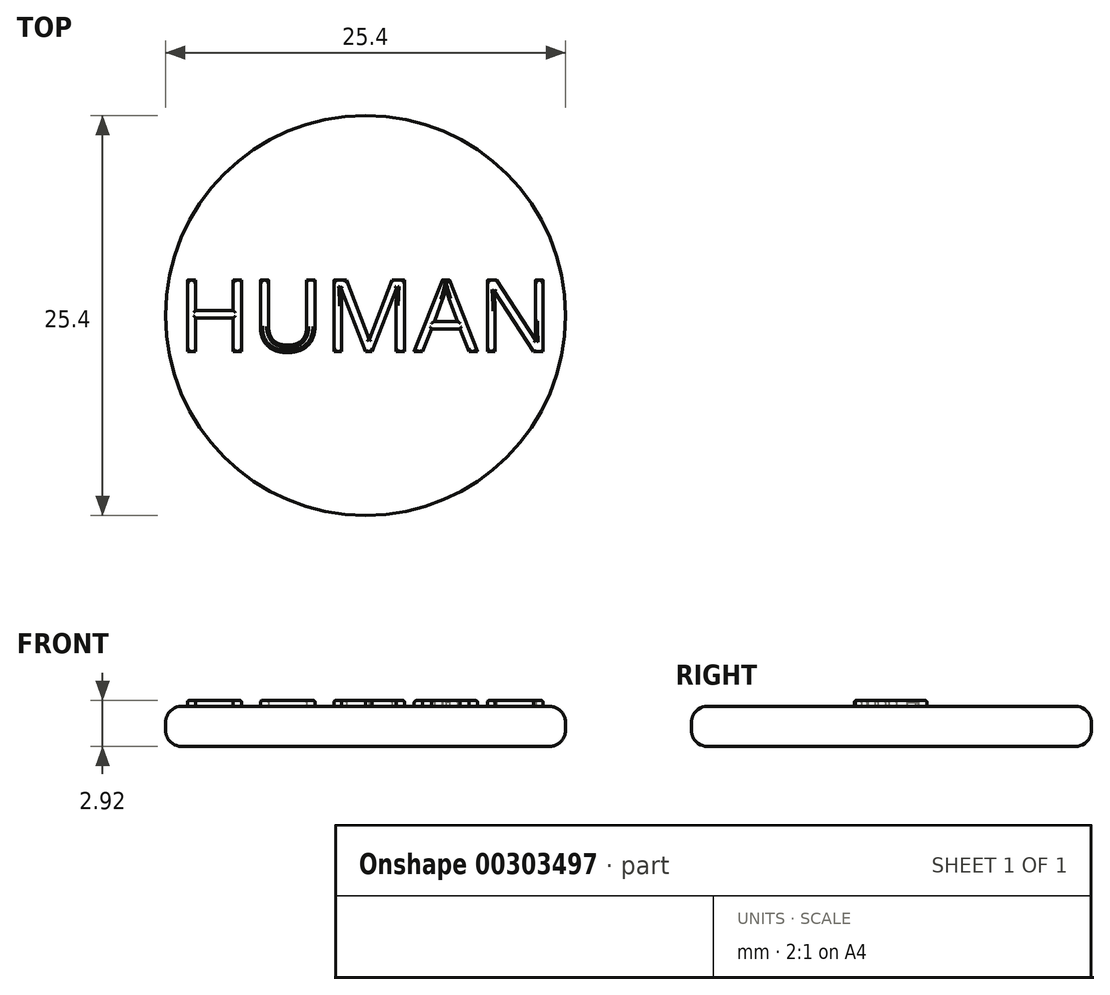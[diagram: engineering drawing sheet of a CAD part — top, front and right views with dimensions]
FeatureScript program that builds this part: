
annotation { "Feature Type Name" : "Feature", "Feature Type Description" : "" }
export const myFeature = defineFeature(function(context is Context, id is Id, definition is map)
    precondition{}
    {
        {
            var Q0;
            Q0=qCreatedBy(makeId("Top.planeOp"),FACE);
            var sketch = newSketch(context, id + "F0", { "sketchPlane" : qUnion([Q0])});
            skCircle(sketch, "E0", {"center": v(0, 0) * mm, "radius": 12.7 * mm});
            skLineSegment(sketch, "E1", {"start": v(0, 0) * mm, "end": v(-11.94, 0) * mm});
            skLineSegment(sketch, "E2", {"start": v(-11.94, 0) * mm, "end": v(-11.94, 2.29) * mm});
            skLineSegment(sketch, "E3", {"start": v(-11.94, 0) * mm, "end": v(-11.94, -2.29) * mm});
            skText(sketch, "E4", { "text": "HUMAN", "fontName": "OpenSans-Regular.ttf"});
            const initialGuessF0  = {"E4": [-0.01194, -0.00229, 1, 0, 0.00457]};
            skSetInitialGuess(sketch, initialGuessF0);
            skSolve(sketch);
        }
        {
            var Q0;
            Q0=makeQuery(id+"F0.imprint","IMPRINT",FACE,{"disambiguationData":[TD([[makeQuery(id+"F0.imprint","IMPRINT",EDGE,{"derivedFrom":sQuery(id+"F0.wireOp",EDGE,"E0")}),1.0]])]});
            var Q1;
            {var subQ0=sQuery(id+"F0.wireOp",EDGE,"E4.sketch_text.stroke-20");Q1=makeQuery(id+"F0.imprint","IMPRINT",FACE,{"disambiguationData":[TD([[makeQuery(id+"F0.imprint","IMPRINT",EDGE,{"derivedFrom":subQ0}),1.0]])]});}
            var Q2;
            {var subQ1=sQuery(id+"F0.wireOp",EDGE,"E4.sketch_text.stroke-27");Q2=makeQuery(id+"F0.imprint","IMPRINT",FACE,{"disambiguationData":[TD([[makeQuery(id+"F0.imprint","IMPRINT",EDGE,{"derivedFrom":subQ1}),1.0]])]});}
            var Q3;
            Q3=makeQuery(id+"F0.imprint","IMPRINT",FACE,{"disambiguationData":[TD([[makeQuery(id+"F0.imprint","IMPRINT",EDGE,{"derivedFrom":sQuery(id+"F0.wireOp",EDGE,"E4.sketch_text.stroke-52")}),1.0]])]});
            extrude(context, id + "F1", {"entities" : qUnion([Q0, Q1, Q2, Q3]), "depth" : 2.54 * mm});
        }
        {
            var Q0;
            {var subQ0=sQuery(id+"F0.wireOp",EDGE,"E4.sketch_text.stroke-6");Q0=makeQuery(id+"F0.imprint","IMPRINT",FACE,{"disambiguationData":[TD([[makeQuery(id+"F0.imprint","IMPRINT",EDGE,{"derivedFrom":subQ0}),-1.0]])]});}
            var Q1;
            {var subQ1=sQuery(id+"F0.wireOp",EDGE,"E4.sketch_text.stroke-0");Q1=makeQuery(id+"F0.imprint","IMPRINT",FACE,{"disambiguationData":[TD([[makeQuery(id+"F0.imprint","IMPRINT",EDGE,{"derivedFrom":subQ1}),-1.0]])]});}
            var Q2;
            {var subQ9=sQuery(id+"F0.wireOp",EDGE,"E4.sketch_text.stroke-13");Q2=makeQuery(id+"F0.imprint","IMPRINT",FACE,{"disambiguationData":[TD([[makeQuery(id+"F0.imprint","IMPRINT",EDGE,{"derivedFrom":subQ9}),-1.0]])]});}
            var Q3;
            {var subQ5=sQuery(id+"F0.wireOp",EDGE,"E4.sketch_text.stroke-18");Q3=makeQuery(id+"F0.imprint","IMPRINT",FACE,{"disambiguationData":[TD([[makeQuery(id+"F0.imprint","IMPRINT",EDGE,{"derivedFrom":subQ5}),-1.0]])]});}
            var Q4;
            {var subQ5=sQuery(id+"F0.wireOp",EDGE,"E4.sketch_text.stroke-25");Q4=makeQuery(id+"F0.imprint","IMPRINT",FACE,{"disambiguationData":[TD([[makeQuery(id+"F0.imprint","IMPRINT",EDGE,{"derivedFrom":subQ5}),-1.0]])]});}
            var Q5;
            {var subQ0=sQuery(id+"F0.wireOp",EDGE,"E4.sketch_text.stroke-27");Q5=makeQuery(id+"F0.imprint","IMPRINT",FACE,{"disambiguationData":[TD([[makeQuery(id+"F0.imprint","IMPRINT",EDGE,{"derivedFrom":subQ0}),-1.0]])]});}
            var Q6;
            {var subQ5=sQuery(id+"F0.wireOp",EDGE,"E4.sketch_text.stroke-30");Q6=makeQuery(id+"F0.imprint","IMPRINT",FACE,{"disambiguationData":[TD([[makeQuery(id+"F0.imprint","IMPRINT",EDGE,{"derivedFrom":subQ5}),-1.0]])]});}
            var Q7;
            {var subQ5=sQuery(id+"F0.wireOp",EDGE,"E4.sketch_text.stroke-34");Q7=makeQuery(id+"F0.imprint","IMPRINT",FACE,{"disambiguationData":[TD([[makeQuery(id+"F0.imprint","IMPRINT",EDGE,{"derivedFrom":subQ5}),-1.0]])]});}
            var Q8;
            Q8=makeQuery(id+"F0.imprint","IMPRINT",FACE,{"disambiguationData":[TD([[makeQuery(id+"F0.imprint","IMPRINT",EDGE,{"derivedFrom":sQuery(id+"F0.wireOp",EDGE,"E4.sketch_text.stroke-44")}),-1.0]])]});
            var Q9;
            Q9=makeQuery(id+"F0.imprint","IMPRINT",FACE,{"disambiguationData":[TD([[makeQuery(id+"F0.imprint","IMPRINT",EDGE,{"derivedFrom":sQuery(id+"F0.wireOp",EDGE,"E4.sketch_text.stroke-57")}),-1.0]])]});
            extrude(context, id + "F2", {"entities" : qUnion([Q0, Q1, Q2, Q3, Q4, Q5, Q6, Q7, Q8, Q9]), "depth" : 2.92 * mm, "hasSecondDirection" : true, "secondDirectionOppositeDirection" : false, "secondDirectionDepth" : 0.64 * mm});
        }
        {
            var Q0;
            Q0=makeQuery(id+"F2.opExtrude","CAP_FACE",FACE,{"disambiguationData":[OSD([sQuery(id+"F0.wireOp",EDGE,"E4.sketch_text.stroke-0"),sQuery(id+"F0.wireOp",EDGE,"E4.sketch_text.stroke-1"),sQuery(id+"F0.wireOp",EDGE,"E4.sketch_text.stroke-2"),sQuery(id+"F0.wireOp",EDGE,"E4.sketch_text.stroke-3"),sQuery(id+"F0.wireOp",EDGE,"E4.sketch_text.stroke-4"),sQuery(id+"F0.wireOp",EDGE,"E4.sketch_text.stroke-5"),sQuery(id+"F0.wireOp",EDGE,"E4.sketch_text.stroke-6"),sQuery(id+"F0.wireOp",EDGE,"E4.sketch_text.stroke-7"),sQuery(id+"F0.wireOp",EDGE,"E4.sketch_text.stroke-8"),sQuery(id+"F0.wireOp",EDGE,"E4.sketch_text.stroke-9"),sQuery(id+"F0.wireOp",EDGE,"E4.sketch_text.stroke-10"),sQuery(id+"F0.wireOp",EDGE,"E4.sketch_text.stroke-11")])],"isStart":false});
            var Q1;
            Q1=makeQuery(id+"F2.opExtrude","CAP_FACE",FACE,{"disambiguationData":[OSD([sQuery(id+"F0.wireOp",EDGE,"E4.sketch_text.stroke-12"),sQuery(id+"F0.wireOp",EDGE,"E4.sketch_text.stroke-13"),sQuery(id+"F0.wireOp",EDGE,"E4.sketch_text.stroke-14"),sQuery(id+"F0.wireOp",EDGE,"E4.sketch_text.stroke-15"),sQuery(id+"F0.wireOp",EDGE,"E4.sketch_text.stroke-16"),sQuery(id+"F0.wireOp",EDGE,"E4.sketch_text.stroke-17"),sQuery(id+"F0.wireOp",EDGE,"E4.sketch_text.stroke-18"),sQuery(id+"F0.wireOp",EDGE,"E4.sketch_text.stroke-19"),sQuery(id+"F0.wireOp",EDGE,"E4.sketch_text.stroke-20"),sQuery(id+"F0.wireOp",EDGE,"E4.sketch_text.stroke-21"),sQuery(id+"F0.wireOp",EDGE,"E4.sketch_text.stroke-22"),sQuery(id+"F0.wireOp",EDGE,"E4.sketch_text.stroke-23"),sQuery(id+"F0.wireOp",EDGE,"E4.sketch_text.stroke-24"),sQuery(id+"F0.wireOp",EDGE,"E4.sketch_text.stroke-25")])],"isStart":false});
            var Q2;
            Q2=makeQuery(id+"F2.opExtrude","CAP_FACE",FACE,{"disambiguationData":[OSD([sQuery(id+"F0.wireOp",EDGE,"E4.sketch_text.stroke-26"),sQuery(id+"F0.wireOp",EDGE,"E4.sketch_text.stroke-27"),sQuery(id+"F0.wireOp",EDGE,"E4.sketch_text.stroke-28"),sQuery(id+"F0.wireOp",EDGE,"E4.sketch_text.stroke-29"),sQuery(id+"F0.wireOp",EDGE,"E4.sketch_text.stroke-30"),sQuery(id+"F0.wireOp",EDGE,"E4.sketch_text.stroke-31"),sQuery(id+"F0.wireOp",EDGE,"E4.sketch_text.stroke-32"),sQuery(id+"F0.wireOp",EDGE,"E4.sketch_text.stroke-33"),sQuery(id+"F0.wireOp",EDGE,"E4.sketch_text.stroke-34"),sQuery(id+"F0.wireOp",EDGE,"E4.sketch_text.stroke-35"),sQuery(id+"F0.wireOp",EDGE,"E4.sketch_text.stroke-36"),sQuery(id+"F0.wireOp",EDGE,"E4.sketch_text.stroke-37"),sQuery(id+"F0.wireOp",EDGE,"E4.sketch_text.stroke-38"),sQuery(id+"F0.wireOp",EDGE,"E4.sketch_text.stroke-39"),sQuery(id+"F0.wireOp",EDGE,"E4.sketch_text.stroke-40"),sQuery(id+"F0.wireOp",EDGE,"E4.sketch_text.stroke-41"),sQuery(id+"F0.wireOp",EDGE,"E4.sketch_text.stroke-42"),sQuery(id+"F0.wireOp",EDGE,"E4.sketch_text.stroke-43")])],"isStart":false});
            var Q3;
            Q3=makeQuery(id+"F2.opExtrude","CAP_FACE",FACE,{"disambiguationData":[OSD([sQuery(id+"F0.wireOp",EDGE,"E4.sketch_text.stroke-44"),sQuery(id+"F0.wireOp",EDGE,"E4.sketch_text.stroke-45"),sQuery(id+"F0.wireOp",EDGE,"E4.sketch_text.stroke-46"),sQuery(id+"F0.wireOp",EDGE,"E4.sketch_text.stroke-47"),sQuery(id+"F0.wireOp",EDGE,"E4.sketch_text.stroke-48"),sQuery(id+"F0.wireOp",EDGE,"E4.sketch_text.stroke-49"),sQuery(id+"F0.wireOp",EDGE,"E4.sketch_text.stroke-50"),sQuery(id+"F0.wireOp",EDGE,"E4.sketch_text.stroke-51"),sQuery(id+"F0.wireOp",EDGE,"E4.sketch_text.stroke-52"),sQuery(id+"F0.wireOp",EDGE,"E4.sketch_text.stroke-53"),sQuery(id+"F0.wireOp",EDGE,"E4.sketch_text.stroke-54"),sQuery(id+"F0.wireOp",EDGE,"E4.sketch_text.stroke-55"),sQuery(id+"F0.wireOp",EDGE,"E4.sketch_text.stroke-56")])],"isStart":false});
            var Q4;
            Q4=makeQuery(id+"F2.opExtrude","CAP_FACE",FACE,{"disambiguationData":[OSD([sQuery(id+"F0.wireOp",EDGE,"E4.sketch_text.stroke-57"),sQuery(id+"F0.wireOp",EDGE,"E4.sketch_text.stroke-58"),sQuery(id+"F0.wireOp",EDGE,"E4.sketch_text.stroke-59"),sQuery(id+"F0.wireOp",EDGE,"E4.sketch_text.stroke-60"),sQuery(id+"F0.wireOp",EDGE,"E4.sketch_text.stroke-61"),sQuery(id+"F0.wireOp",EDGE,"E4.sketch_text.stroke-62"),sQuery(id+"F0.wireOp",EDGE,"E4.sketch_text.stroke-63"),sQuery(id+"F0.wireOp",EDGE,"E4.sketch_text.stroke-64"),sQuery(id+"F0.wireOp",EDGE,"E4.sketch_text.stroke-65"),sQuery(id+"F0.wireOp",EDGE,"E4.sketch_text.stroke-66"),sQuery(id+"F0.wireOp",EDGE,"E4.sketch_text.stroke-67"),sQuery(id+"F0.wireOp",EDGE,"E4.sketch_text.stroke-68"),sQuery(id+"F0.wireOp",EDGE,"E4.sketch_text.stroke-69"),sQuery(id+"F0.wireOp",EDGE,"E4.sketch_text.stroke-70"),sQuery(id+"F0.wireOp",EDGE,"E4.sketch_text.stroke-71")])],"isStart":false});
            fillet(context, id + "F3", {"entities" : qUnion([Q0, Q1, Q2, Q3, Q4]), "radius" : 0.13 * mm, "tangentPropagation" : true, "allowEdgeOverflow" : false});
        }
        {
            var Q0;
            Q0=makeQuery(id+"F1.opExtrude","CAP_EDGE",EDGE,{"disambiguationData":[OSD([sQuery(id+"F0.wireOp",EDGE,"E0")])],"isStart":false});
            var Q1;
            Q1=makeQuery(id+"F1.opExtrude","SWEPT_FACE",FACE,{"disambiguationData":[OSD([sQuery(id+"F0.wireOp",EDGE,"E0")])]});
            fillet(context, id + "F4", {"entities" : qUnion([Q0, Q1]), "radius" : 1.02 * mm, "tangentPropagation" : true, "allowEdgeOverflow" : false});
        }
        {
            var Q0;
            {var subQ0=sQuery(id+"F0.wireOp",EDGE,"E4.sketch_text.stroke-6");Q0=makeQuery(id+"F0.imprint","IMPRINT",FACE,{"disambiguationData":[TD([[makeQuery(id+"F0.imprint","IMPRINT",EDGE,{"derivedFrom":subQ0}),-1.0]])]});}
            var Q1;
            {var subQ1=sQuery(id+"F0.wireOp",EDGE,"E4.sketch_text.stroke-0");Q1=makeQuery(id+"F0.imprint","IMPRINT",FACE,{"disambiguationData":[TD([[makeQuery(id+"F0.imprint","IMPRINT",EDGE,{"derivedFrom":subQ1}),-1.0]])]});}
            var Q2;
            {var subQ9=sQuery(id+"F0.wireOp",EDGE,"E4.sketch_text.stroke-13");Q2=makeQuery(id+"F0.imprint","IMPRINT",FACE,{"disambiguationData":[TD([[makeQuery(id+"F0.imprint","IMPRINT",EDGE,{"derivedFrom":subQ9}),-1.0]])]});}
            var Q3;
            {var subQ5=sQuery(id+"F0.wireOp",EDGE,"E4.sketch_text.stroke-18");Q3=makeQuery(id+"F0.imprint","IMPRINT",FACE,{"disambiguationData":[TD([[makeQuery(id+"F0.imprint","IMPRINT",EDGE,{"derivedFrom":subQ5}),-1.0]])]});}
            var Q4;
            {var subQ5=sQuery(id+"F0.wireOp",EDGE,"E4.sketch_text.stroke-30");Q4=makeQuery(id+"F0.imprint","IMPRINT",FACE,{"disambiguationData":[TD([[makeQuery(id+"F0.imprint","IMPRINT",EDGE,{"derivedFrom":subQ5}),-1.0]])]});}
            var Q5;
            {var subQ0=sQuery(id+"F0.wireOp",EDGE,"E4.sketch_text.stroke-27");Q5=makeQuery(id+"F0.imprint","IMPRINT",FACE,{"disambiguationData":[TD([[makeQuery(id+"F0.imprint","IMPRINT",EDGE,{"derivedFrom":subQ0}),-1.0]])]});}
            var Q6;
            {var subQ5=sQuery(id+"F0.wireOp",EDGE,"E4.sketch_text.stroke-34");Q6=makeQuery(id+"F0.imprint","IMPRINT",FACE,{"disambiguationData":[TD([[makeQuery(id+"F0.imprint","IMPRINT",EDGE,{"derivedFrom":subQ5}),-1.0]])]});}
            var Q7;
            Q7=makeQuery(id+"F0.imprint","IMPRINT",FACE,{"disambiguationData":[TD([[makeQuery(id+"F0.imprint","IMPRINT",EDGE,{"derivedFrom":sQuery(id+"F0.wireOp",EDGE,"E4.sketch_text.stroke-44")}),-1.0]])]});
            var Q8;
            Q8=makeQuery(id+"F0.imprint","IMPRINT",FACE,{"disambiguationData":[TD([[makeQuery(id+"F0.imprint","IMPRINT",EDGE,{"derivedFrom":sQuery(id+"F0.wireOp",EDGE,"E4.sketch_text.stroke-57")}),-1.0]])]});
            var Q9;
            {var subQ5=sQuery(id+"F0.wireOp",EDGE,"E4.sketch_text.stroke-25");Q9=makeQuery(id+"F0.imprint","IMPRINT",FACE,{"disambiguationData":[TD([[makeQuery(id+"F0.imprint","IMPRINT",EDGE,{"derivedFrom":subQ5}),-1.0]])]});}
            extrude(context, id + "F5", {"entities" : qUnion([Q0, Q1, Q2, Q3, Q4, Q5, Q6, Q7, Q8, Q9]), "operationType" : NewBodyOperationType.ADD, "depth" : 0.64 * mm});
        }
    });
